# Revit family: Window_Shade-Draper-FlexShade_Zip
name_source: partatom
category: Specialty Equipment
units: mm (PartAtom-declared; Revit-internal decimal feet)

## family parameters
Always vertical = Yes
Classification Number = 23.30.20.11
Cut with Voids When Loaded = No
Enable Cutting in Views = No
Maintain Annotation Orientation = No
Part Type = Normal
Room Calculation Point = No
Round Connector Dimension = Use Diameter
Shared = No
Work Plane-Based = No

## types (2) — shared parameters
Casing = Metal - Draper - Silver
Default Elevation = 0' - 0"
Description = Wind Resistant Roller Shade
Manufacturer = Draper
Model = FlexShade
Product Name = FlexShade Zip
Shade Fabric = Fabric - Draper - Screen
URL = http://www.draperinc.com
Wind Note = Very wind resistant.  Wind tunnel tested up to 90 MPH.

## per-type parameters (varying)
| type | Product Page URL |
| 105 Style Headbox | http://www.draperinc.com |
| 125 Style Headbox | www.draperinc.com/go/FlexShadeZip.htm |

type visibility flags: 2 boolean params named "<type name>" — each type sets only its own to Yes (folded from table)

## geometry (parser evidence)
native form markers: Blend x13, Sweep x3
no freeform markers — native parametric forms only
